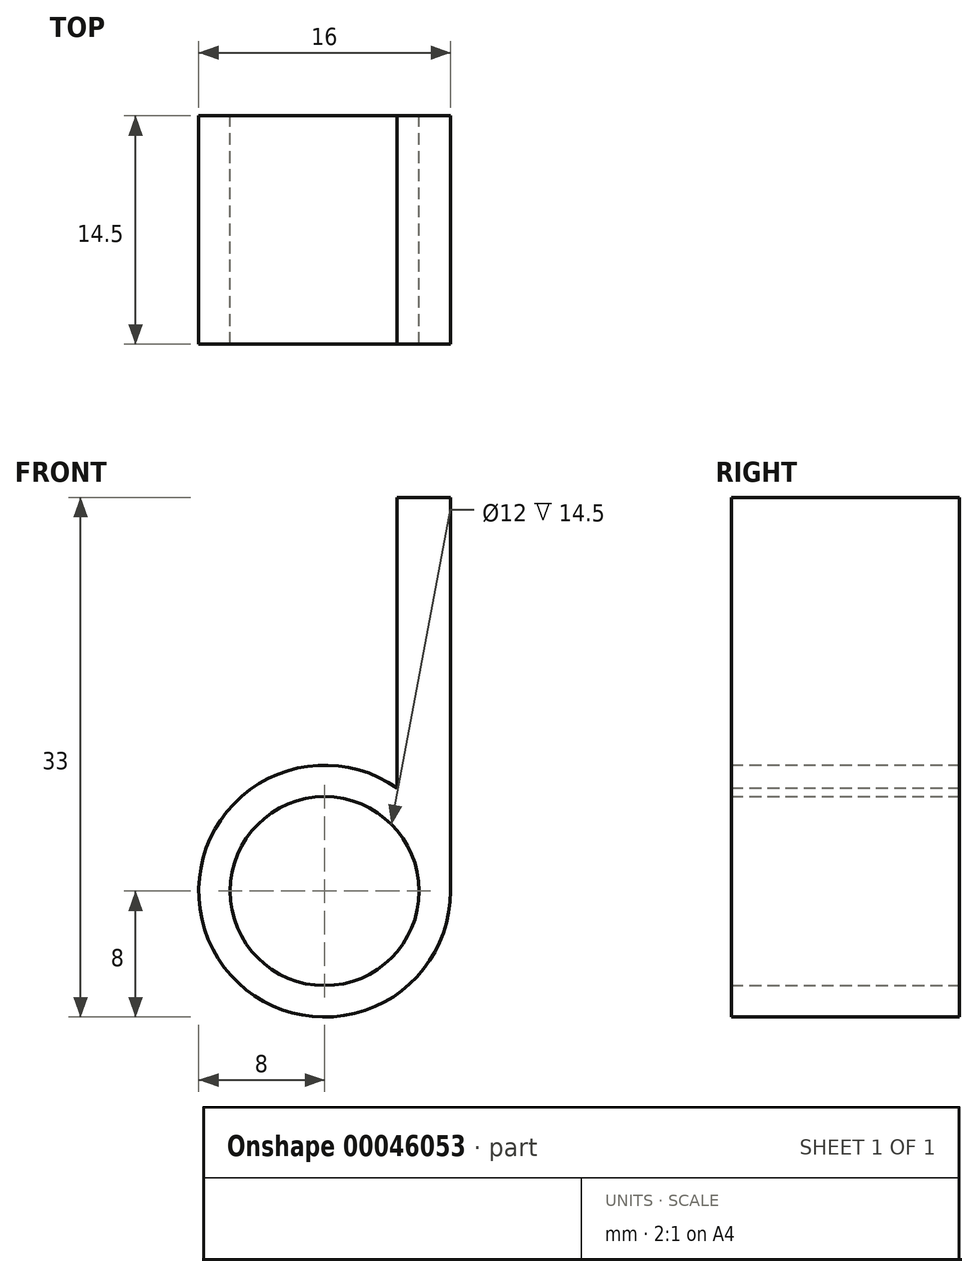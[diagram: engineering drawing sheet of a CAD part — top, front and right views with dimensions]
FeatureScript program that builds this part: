
annotation { "Feature Type Name" : "Feature", "Feature Type Description" : "" }
export const myFeature = defineFeature(function(context is Context, id is Id, definition is map)
    precondition{}
    {
        {
            var Q0;
            Q0=qCreatedBy(makeId("Front.planeOp"),FACE);
            var sketch = newSketch(context, id + "F0", { "sketchPlane" : qUnion([Q0])});
            skCircle(sketch, "E0", {"center": v(0, 0) * mm, "radius": 6 * mm});
            skCircle(sketch, "E1", {"center": v(0, 0) * mm, "radius": 8 * mm});
            skLineSegment(sketch, "E2", {"start": v(8, 0) * mm, "end": v(8, 25) * mm});
            skLineSegment(sketch, "E3", {"start": v(8, 25) * mm, "end": v(4.6, 25) * mm});
            skLineSegment(sketch, "E4", {"start": v(4.6, 25) * mm, "end": v(4.6, 3.85) * mm});
            skLineSegment(sketch, "E5", {"start": v(-6.23, 5.02) * mm, "end": v(0, 0) * mm, "construction": true});
            skSolve(sketch);
        }
        {
            var Q0;
            Q0 = qSketchRegion(id + "F0", true);
            extrude(context, id + "F1", {"entities" : qUnion([Q0]), "depth" : 14.5 * mm});
        }
    });
